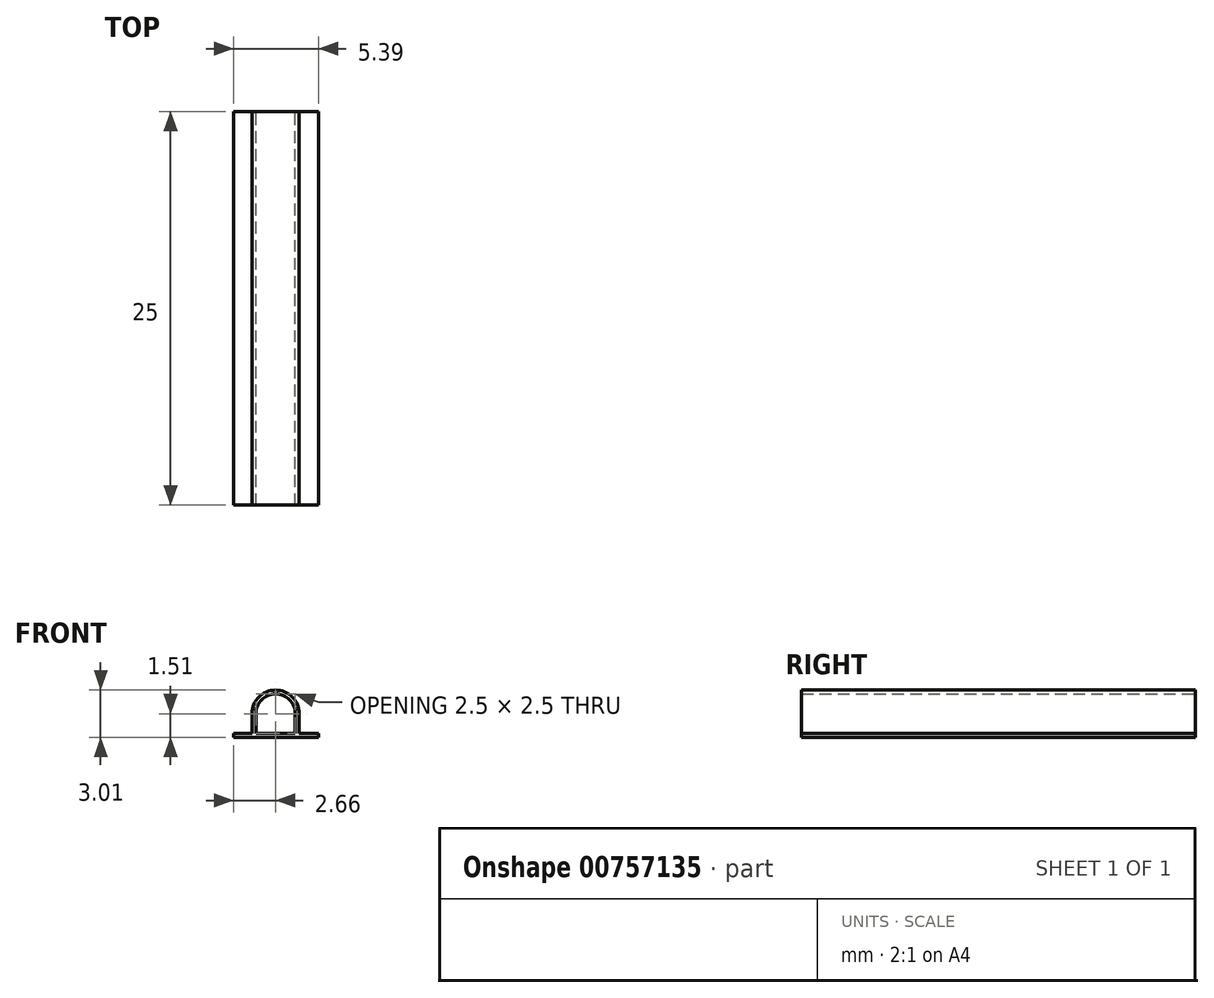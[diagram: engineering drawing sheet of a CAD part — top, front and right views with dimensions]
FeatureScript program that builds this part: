
annotation { "Feature Type Name" : "Feature", "Feature Type Description" : "" }
export const myFeature = defineFeature(function(context is Context, id is Id, definition is map)
    precondition{}
    {
        {
            var Q0;
            Q0=qCreatedBy(makeId("Front.planeOp"),FACE);
            var sketch = newSketch(context, id + "F0", { "sketchPlane" : qUnion([Q0])});
            skArc(sketch, "E0", {"start": v(1.25, 0) * mm, "mid": v(0, 1.25) * mm, "end": v(-1.25, 0) * mm});
            skArc(sketch, "E1", {"start": v(1.5, 0) * mm, "mid": v(0, 1.5) * mm, "end": v(-1.5, 0) * mm});
            skLineSegment(sketch, "E2", {"start": v(-1.5, 0) * mm, "end": v(-1.25, 0) * mm});
            skLineSegment(sketch, "E3", {"start": v(1.25, 0) * mm, "end": v(1.5, 0) * mm});
            skLineSegment(sketch, "E4", {"start": v(0, 1.25) * mm, "end": v(0, -1.25) * mm, "construction": true});
            skLineSegment(sketch, "E5", {"start": v(0, -1.25) * mm, "end": v(-3.37, -1.25) * mm, "construction": true});
            skLineSegment(sketch, "E6", {"start": v(-3.37, -1.25) * mm, "end": v(4.71, -1.25) * mm, "construction": true});
            skLineSegment(sketch, "E7", {"start": v(-1.25, 0) * mm, "end": v(-1.25, -1.25) * mm});
            skLineSegment(sketch, "E8", {"start": v(-1.5, 0) * mm, "end": v(-1.5, -1.25) * mm});
            skLineSegment(sketch, "E9", {"start": v(-1.5, -1.25) * mm, "end": v(-1.25, -1.25) * mm});
            skLineSegment(sketch, "E10", {"start": v(1.25, 0) * mm, "end": v(1.25, -1.25) * mm});
            skLineSegment(sketch, "E11", {"start": v(1.5, 0) * mm, "end": v(1.5, -1.25) * mm});
            skLineSegment(sketch, "E12", {"start": v(1.5, -1.25) * mm, "end": v(1.25, -1.25) * mm});
            skLineSegment(sketch, "E13.bottom", {"start": v(-2.66, -1.25) * mm, "end": v(2.73, -1.25) * mm});
            skLineSegment(sketch, "E13.top", {"start": v(-2.66, -1.5) * mm, "end": v(2.73, -1.5) * mm});
            skLineSegment(sketch, "E13.left", {"start": v(-2.66, -1.25) * mm, "end": v(-2.66, -1.5) * mm});
            skLineSegment(sketch, "E13.right", {"start": v(2.73, -1.25) * mm, "end": v(2.73, -1.5) * mm});
            skSolve(sketch);
        }
        {
            var Q0;
            Q0 = qSketchRegion(id + "F0", true);
            var Q1;
            Q1 = qSketchRegion(id + "FTwcijDxjN4JesB_0", true);
            extrude(context, id + "F1", {"entities" : qUnion([Q0, Q1]), "depth" : 25 * mm, "offsetDistance" : 25 * mm});
        }
    });
